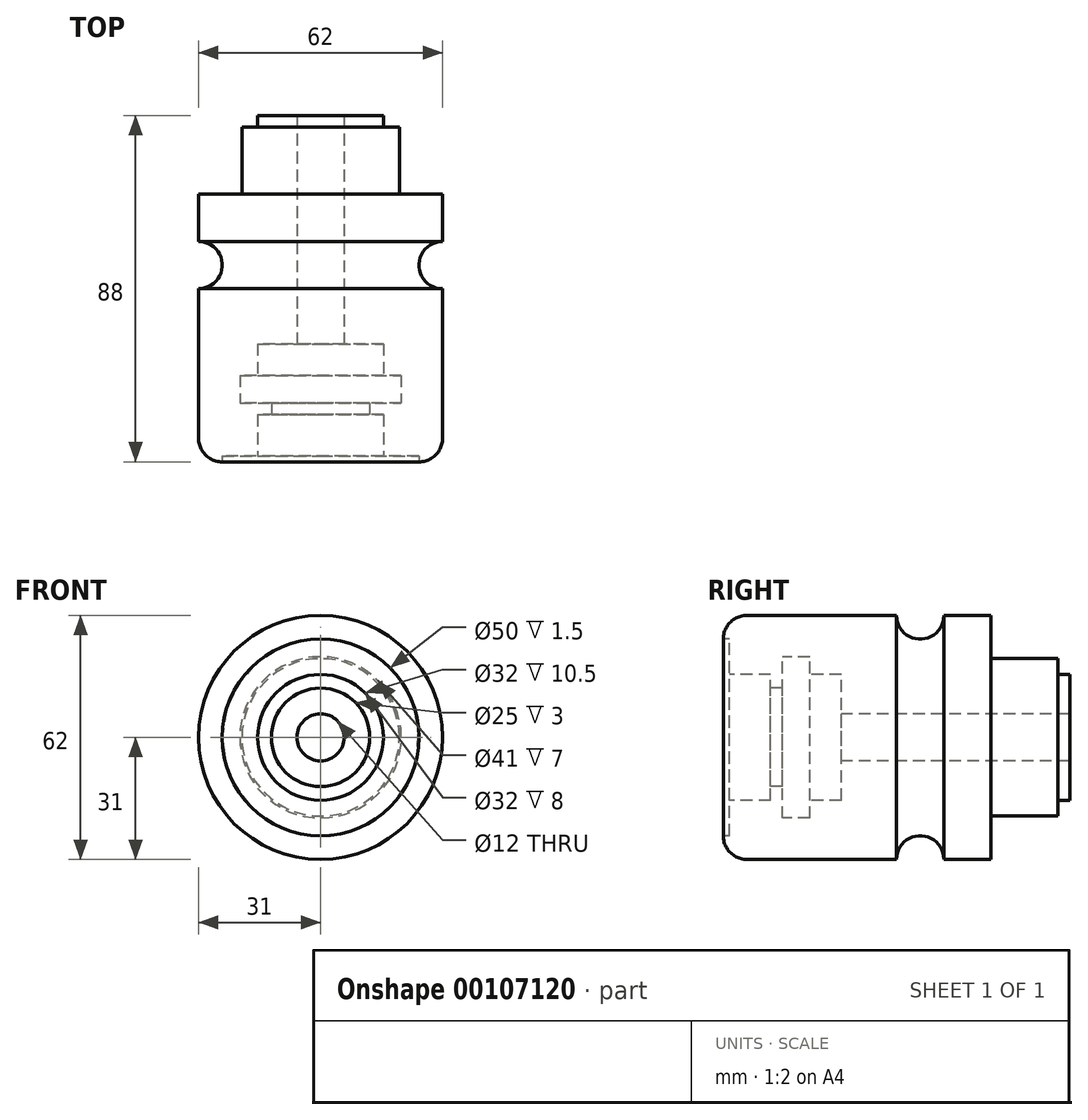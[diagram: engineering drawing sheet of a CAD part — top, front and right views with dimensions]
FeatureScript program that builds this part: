
annotation { "Feature Type Name" : "Feature", "Feature Type Description" : "" }
export const myFeature = defineFeature(function(context is Context, id is Id, definition is map)
    precondition{}
    {
        {
            var Q0;
            Q0=qCreatedBy(makeId("Right.planeOp"),FACE);
            var sketch = newSketch(context, id + "F0", { "sketchPlane" : qUnion([Q0])});
            skLineSegment(sketch, "E0", {"start": v(6, 31) * mm, "end": v(44, 31) * mm});
            skLineSegment(sketch, "E1", {"start": v(56, 31) * mm, "end": v(68, 31) * mm});
            skLineSegment(sketch, "E2", {"start": v(68, 31) * mm, "end": v(68, 20) * mm});
            skLineSegment(sketch, "E3", {"start": v(68, 20) * mm, "end": v(85, 20) * mm});
            skLineSegment(sketch, "E4", {"start": v(85, 20) * mm, "end": v(85, 16) * mm});
            skLineSegment(sketch, "E5", {"start": v(85, 16) * mm, "end": v(88, 16) * mm});
            skLineSegment(sketch, "E6", {"start": v(88, 16) * mm, "end": v(88, 6) * mm});
            skLineSegment(sketch, "E7", {"start": v(88, 6) * mm, "end": v(30, 6) * mm});
            skLineSegment(sketch, "E8", {"start": v(30, 6) * mm, "end": v(30, 16) * mm});
            skLineSegment(sketch, "E9", {"start": v(30, 16) * mm, "end": v(22, 16) * mm});
            skLineSegment(sketch, "E10", {"start": v(22, 16) * mm, "end": v(22, 20.5) * mm});
            skLineSegment(sketch, "E11", {"start": v(22, 20.5) * mm, "end": v(15, 20.5) * mm});
            skLineSegment(sketch, "E12", {"start": v(15, 20.5) * mm, "end": v(15, 12.5) * mm});
            skLineSegment(sketch, "E13", {"start": v(15, 12.5) * mm, "end": v(12, 12.5) * mm});
            skLineSegment(sketch, "E14", {"start": v(12, 12.5) * mm, "end": v(12, 16) * mm});
            skLineSegment(sketch, "E15", {"start": v(0, 16) * mm, "end": v(0, 0) * mm, "construction": true});
            skLineSegment(sketch, "E16", {"start": v(0, 0) * mm, "end": v(88, 0) * mm, "construction": true});
            skArc(sketch, "E17", {"start": v(44, 31) * mm, "mid": v(50, 24.97) * mm, "end": v(56, 31) * mm});
            skLineSegment(sketch, "E18", {"start": v(12, 16) * mm, "end": v(1.5, 16) * mm});
            skLineSegment(sketch, "E19", {"start": v(1.5, 16) * mm, "end": v(1.5, 25) * mm});
            skLineSegment(sketch, "E20", {"start": v(1.5, 25) * mm, "end": v(0, 25) * mm});
            skLineSegment(sketch, "E21", {"start": v(0, 25) * mm, "end": v(0, 16) * mm, "construction": true});
            skArc(sketch, "E22", {"start": v(6, 31) * mm, "mid": v(1.76, 29.24) * mm, "end": v(0, 25) * mm});
            skSolve(sketch);
        }
        {
            var Q0;
            Q0 = qSketchRegion(id + "F0", true);
            var Q1;
            Q1=sQuery(id+"F0.wireOp",EDGE,"E16");
            revolve(context, id + "F1", {"entities" : qUnion([Q0]), "axis" : qUnion([Q1]), "revolveType" : RevolveType.FULL});
        }
    });
